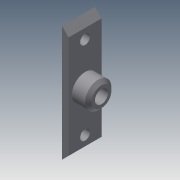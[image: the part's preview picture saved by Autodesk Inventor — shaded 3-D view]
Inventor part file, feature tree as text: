
AUTODESK INVENTOR PART (.ipt)
format: ipt  version: 2015 (Build 190159000, 159)  size: 123,904 bytes
history: native  units: mm
features: extrude x4, sketch x4, chamfer x2
ambient origin geometry x8: Origin, YZ Plane, XZ Plane, XY Plane, X Axis, Y Axis, Z Axis, Center Point
bodies: Solid1 (feature_tree)
feature tree (10):
  extrude  "Extrusion1"  Depth=10.0mm
  extrude  "Extrusion2"  Depth=2.0mm
  extrude  "Extrusion3"  Depth=4.0mm
  extrude  "Extrusion4"  Depth=5.0mm
  chamfer  "Chamfer1"  Distance=5.0mm
  chamfer  "Chamfer2"  Distance=3.0mm
  sketch  "Sketch1"  dims[d0=35.186mm d2=10.0mm]
  sketch  "Sketch2"  dims[d3=2.0mm d4=0.0mm d5=8.0mm]
  sketch  "Sketch3"  dims[d6=5.0mm d7=0.0mm d8=4.0mm]
  sketch  "Sketch4"  dims[d9=7.0mm d10=0.0mm d11=5.0mm d12=5.0mm d13=3.0mm d14=3.0mm d15=2.0mm d16=0.0mm d17=1.0mm d18=2.0mm d19=45.0deg d20=2.0mm d21=2.0mm d22=45.0deg]
